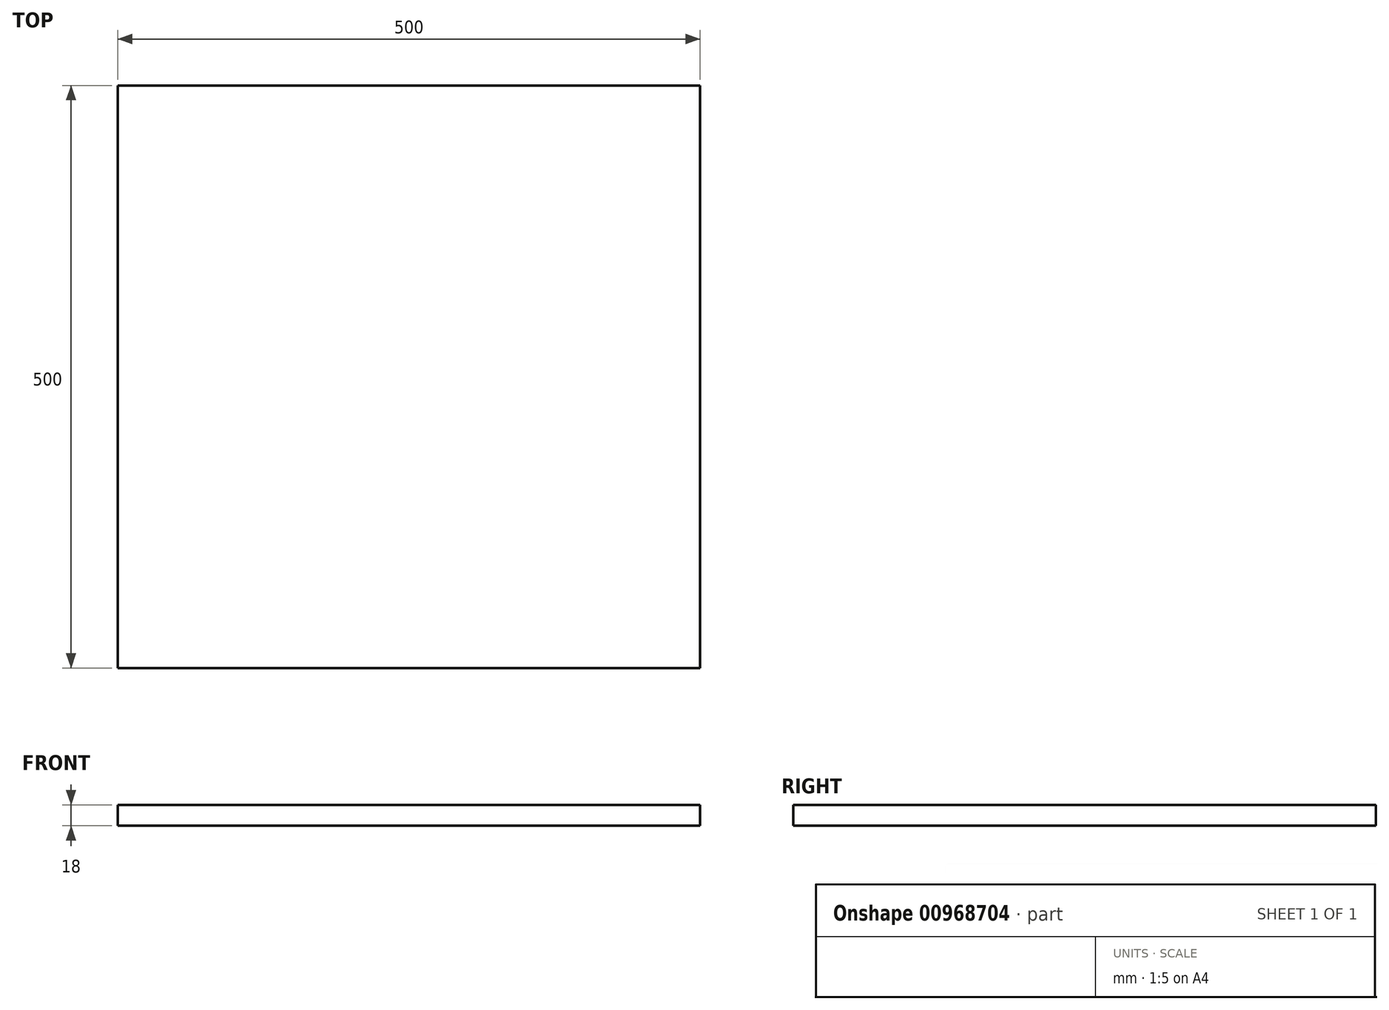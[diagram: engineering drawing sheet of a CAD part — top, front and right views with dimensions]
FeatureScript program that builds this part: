
annotation { "Feature Type Name" : "Feature", "Feature Type Description" : "" }
export const myFeature = defineFeature(function(context is Context, id is Id, definition is map)
    precondition{}
    {
        {
            var Q0;
            Q0=qCreatedBy(makeId("Top.planeOp"),FACE);
            var sketch = newSketch(context, id + "F0", { "sketchPlane" : qUnion([Q0])});
            skLineSegment(sketch, "E0.bottom", {"start": v(335.09, 347.92) * mm, "end": v(-164.91, 347.92) * mm});
            skLineSegment(sketch, "E0.top", {"start": v(335.09, -152.08) * mm, "end": v(-164.91, -152.08) * mm});
            skLineSegment(sketch, "E0.left", {"start": v(335.09, 347.92) * mm, "end": v(335.09, -152.08) * mm});
            skLineSegment(sketch, "E0.right", {"start": v(-164.91, 347.92) * mm, "end": v(-164.91, -152.08) * mm});
            skPoint(sketch, "E0.middle", {"position": v(85.09, 97.92) * mm});
            skSolve(sketch);
        }
        {
            var Q0;
            Q0 = qSketchRegion(id + "F0", true);
            extrude(context, id + "F1", {"entities" : qUnion([Q0]), "depth" : 18 * mm, "offsetDistance" : 25 * mm});
        }
    });
